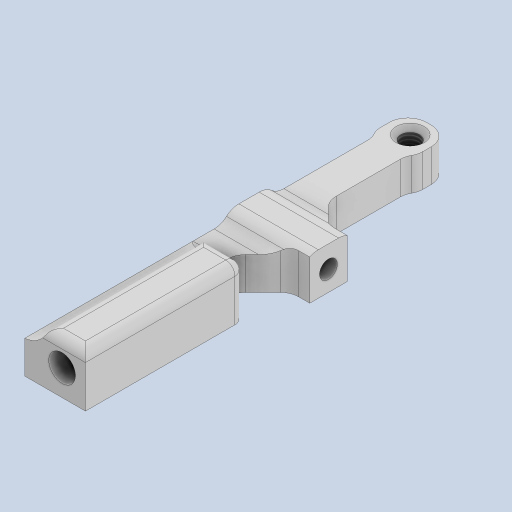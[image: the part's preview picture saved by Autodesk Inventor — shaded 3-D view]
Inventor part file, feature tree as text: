
AUTODESK INVENTOR PART (.ipt)
format: ipt  version: 2023 (Build 270158000, 158)  size: 343,040 bytes
history: native  units: mm
features: extrude x13, sketch x13, fillet x8, other x3, thread x3, chamfer x2, projected_geometry x1
ambient origin geometry x8: Origin, YZ Plane, XZ Plane, XY Plane, X Axis, Y Axis, Z Axis, Center Point
bodies: Body1 (feature_tree)
feature tree (43):
  other  "Твердое тело1"
  extrude  "Выдавливание1"  Depth=3.5mm
  extrude  "Выдавливание2"  Depth=70.0mm
  extrude  "Выдавливание3"  Depth=3.5mm TaperAngle=0.0deg
  chamfer  "Фаска1"  Distance=3.0mm
  fillet  "Сопряжение3"  Radius=0.5mm
  fillet  "Сопряжение4"  Radius=3.5mm
  extrude  "Выдавливание4"  Depth=4.5mm
  extrude  "Выдавливание5"  Depth=3.0mm
  thread  "Резьба1"
  thread  "Резьба2"
  thread  "Резьба3"
  other  "РабПлоскость1"
  extrude  "Выдавливание8"  Depth=0.5mm
  extrude  "Выдавливание9"  Depth=3.5mm
  other  "РабПлоскость2"
  extrude  "Выдавливание11"  Depth=3.5mm TaperAngle=0.0deg
  extrude  "Выдавливание12"  Depth=3.5mm
  extrude  "Выдавливание13"  Depth=3.0mm
  extrude  "Выдавливание15"  TaperAngle=0.0deg  [1 undecoded]
  fillet  "Сопряжение18"  Radius=2.0mm
  fillet  "Сопряжение20"  Radius=3.0mm
  fillet  "Сопряжение21"  Radius=2.0mm
  fillet  "Сопряжение22"  Radius=3.5mm
  extrude  "Выдавливание16"  Depth=2.0mm TaperAngle=45.0deg
  chamfer  "Фаска6"  Distance=2.0mm
  fillet  "Сопряжение23"  Radius=2.0mm
  fillet  "Сопряжение24"  Radius=2.0mm
  extrude  "Выдавливание17"  Depth=3.5mm TaperAngle=0.0deg
  sketch  "Эскиз1"
  sketch  "Эскиз2"
  sketch  "Эскиз3"
  sketch  "Эскиз4"
  sketch  "Эскиз5"
  sketch  "Эскиз8"
  sketch  "Эскиз9"
  sketch  "Эскиз11"
  sketch  "Эскиз12"
  sketch  "Эскиз13"
  sketch  "Эскиз15"
  sketch  "Эскиз16"
  projected_geometry  "Спроецированная петля1"
  sketch  "Эскиз17"
note: 1 required parameter value undecoded (feature->parameter linkage not recoverable at this tier; creation-order binding heuristic only, values carry confidence <= 0.55)
